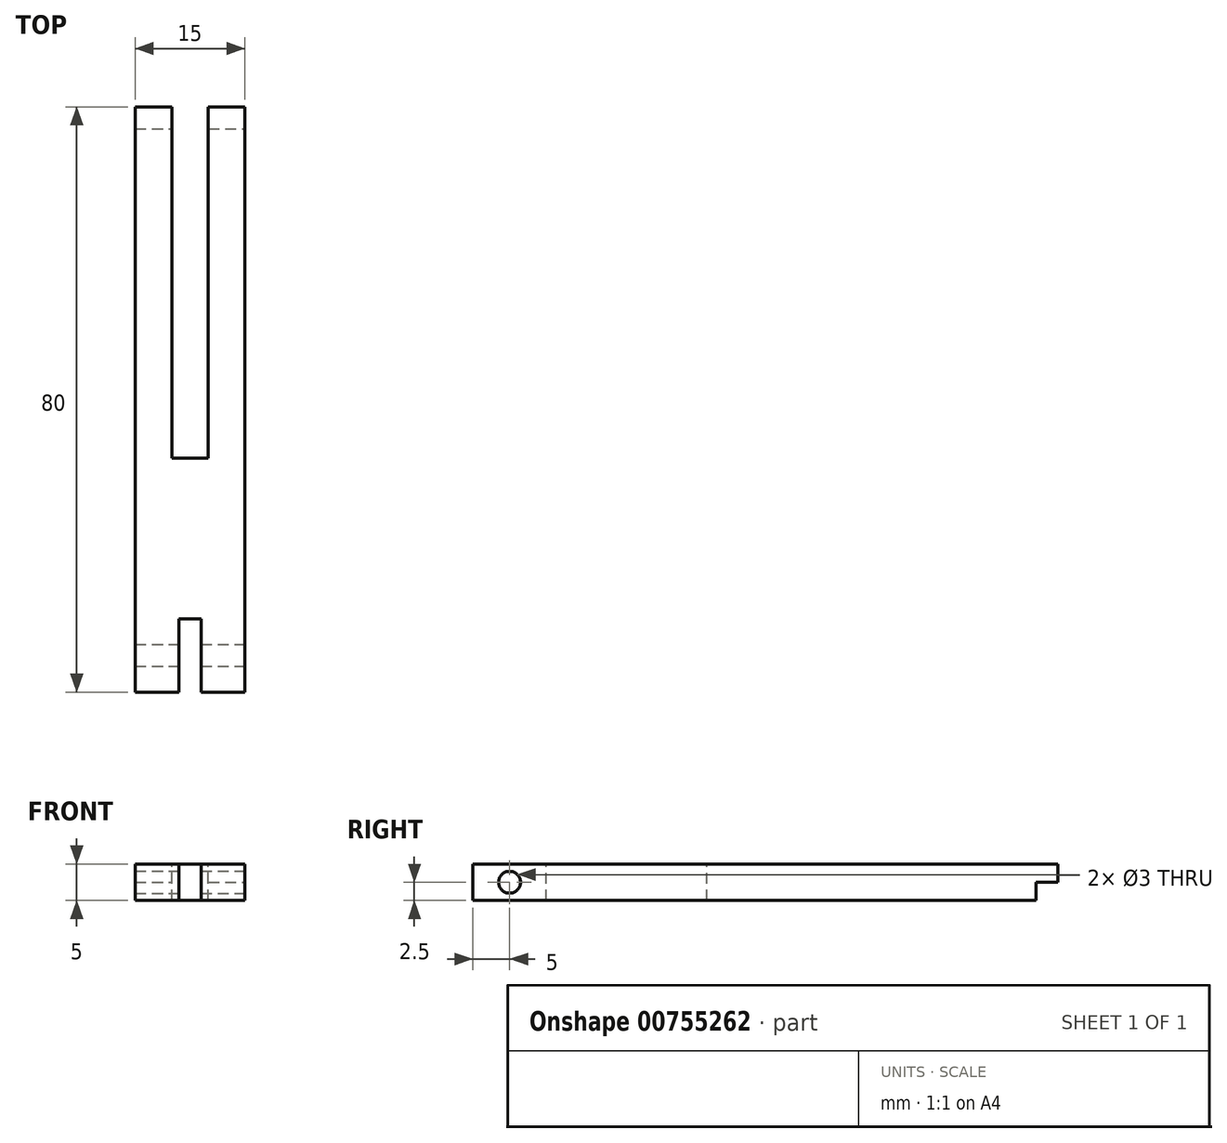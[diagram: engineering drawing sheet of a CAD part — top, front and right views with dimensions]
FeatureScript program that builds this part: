
annotation { "Feature Type Name" : "Feature", "Feature Type Description" : "" }
export const myFeature = defineFeature(function(context is Context, id is Id, definition is map)
    precondition{}
    {
        {
            var Q0;
            Q0=qCreatedBy(makeId("Top.planeOp"),FACE);
            var sketch = newSketch(context, id + "F0", { "sketchPlane" : qUnion([Q0])});
            skLineSegment(sketch, "E0.bottom", {"start": v(-7.5, 80) * mm, "end": v(7.5, 80) * mm});
            skLineSegment(sketch, "E0.top", {"start": v(-7.5, 0) * mm, "end": v(7.5, 0) * mm});
            skLineSegment(sketch, "E0.left", {"start": v(-7.5, 80) * mm, "end": v(-7.5, 0) * mm});
            skLineSegment(sketch, "E0.right", {"start": v(7.5, 80) * mm, "end": v(7.5, 0) * mm});
            skPoint(sketch, "E1", {"position": v(0, 0) * mm});
            skSolve(sketch);
        }
        {
            var Q0;
            Q0 = qSketchRegion(id + "F0", true);
            extrude(context, id + "F1", {"entities" : qUnion([Q0]), "depth" : 5 * mm, "offsetDistance" : 25 * mm});
        }
        {
            var Q0;
            Q0=makeQuery(id+"F1.opExtrude","CAP_FACE",FACE,{"disambiguationData":[OSD([sQuery(id+"F0.wireOp",EDGE,"E0.bottom"),sQuery(id+"F0.wireOp",EDGE,"E0.top"),sQuery(id+"F0.wireOp",EDGE,"E0.left"),sQuery(id+"F0.wireOp",EDGE,"E0.right")])],"isStart":false});
            var sketch = newSketch(context, id + "F2", { "sketchPlane" : qUnion([Q0])});
            skLineSegment(sketch, "E2.bottom", {"start": v(-2.5, 80) * mm, "end": v(2.5, 80) * mm});
            skLineSegment(sketch, "E2.top", {"start": v(-2.5, 32) * mm, "end": v(2.5, 32) * mm});
            skLineSegment(sketch, "E2.left", {"start": v(-2.5, 80) * mm, "end": v(-2.5, 32) * mm});
            skLineSegment(sketch, "E2.right", {"start": v(2.5, 80) * mm, "end": v(2.5, 32) * mm});
            skPoint(sketch, "E3", {"position": v(0, 32) * mm});
            skSolve(sketch);
        }
        {
            var Q0;
            Q0=makeQuery(id+"F2.imprint","IMPRINT",FACE,{"disambiguationData":[TD([[makeQuery(id+"F2.imprint","IMPRINT",EDGE,{"derivedFrom":sQuery(id+"F2.wireOp",EDGE,"E2.bottom")}),-1.0]])]});
            extrude(context, id + "F3", {"entities" : qUnion([Q0]), "operationType" : NewBodyOperationType.REMOVE, "oppositeDirection" : true, "depth" : 25 * mm, "offsetDistance" : 25 * mm});
        }
        {
            var Q0;
            {var subQ1=sQuery(id+"F0.wireOp",EDGE,"E0.left");var subQ3=sQuery(id+"F0.wireOp",EDGE,"E0.bottom");Q0=makeQuery(id+"F3.boolean.opBoolean","SPLIT",FACE,{"disambiguationData":[TD([makeQuery(id+"F1.opExtrude","SWEPT_FACE",FACE,{"disambiguationData":[OSD([subQ1])]})])],"derivedFrom":makeQuery(id+"F1.opExtrude","SWEPT_FACE",FACE,{"disambiguationData":[OSD([subQ3])]})});}
            var sketch = newSketch(context, id + "F4", { "sketchPlane" : qUnion([Q0])});
            skLineSegment(sketch, "E4.bottom", {"start": v(7.5, 2.5) * mm, "end": v(2.5, 2.5) * mm});
            skLineSegment(sketch, "E4.top", {"start": v(7.5, 0) * mm, "end": v(2.5, 0) * mm});
            skLineSegment(sketch, "E4.left", {"start": v(7.5, 2.5) * mm, "end": v(7.5, 0) * mm});
            skLineSegment(sketch, "E4.right", {"start": v(2.5, 2.5) * mm, "end": v(2.5, 0) * mm});
            skSolve(sketch);
        }
        {
            var Q0;
            Q0=makeQuery(id+"F4.imprint","IMPRINT",FACE,{"disambiguationData":[TD([[makeQuery(id+"F4.imprint","IMPRINT",EDGE,{"derivedFrom":sQuery(id+"F4.wireOp",EDGE,"E4.bottom")}),1.0]])]});
            extrude(context, id + "F5", {"entities" : qUnion([Q0]), "operationType" : NewBodyOperationType.REMOVE, "oppositeDirection" : true, "depth" : 3 * mm, "offsetDistance" : 25 * mm});
        }
        {
            var Q0;
            {var subQ0=sQuery(id+"F0.wireOp",EDGE,"E0.right");var subQ3=sQuery(id+"F0.wireOp",EDGE,"E0.bottom");Q0=makeQuery(id+"F3.boolean.opBoolean","SPLIT",FACE,{"disambiguationData":[TD([makeQuery(id+"F1.opExtrude","SWEPT_FACE",FACE,{"disambiguationData":[OSD([subQ0])]})])],"derivedFrom":makeQuery(id+"F1.opExtrude","SWEPT_FACE",FACE,{"disambiguationData":[OSD([subQ3])]})});}
            var sketch = newSketch(context, id + "F6", { "sketchPlane" : qUnion([Q0])});
            skLineSegment(sketch, "E5.bottom", {"start": v(-2.5, 0) * mm, "end": v(-7.5, 0) * mm});
            skLineSegment(sketch, "E5.top", {"start": v(-2.5, 2.5) * mm, "end": v(-7.5, 2.5) * mm});
            skLineSegment(sketch, "E5.left", {"start": v(-2.5, 0) * mm, "end": v(-2.5, 2.5) * mm});
            skLineSegment(sketch, "E5.right", {"start": v(-7.5, 0) * mm, "end": v(-7.5, 2.5) * mm});
            skSolve(sketch);
        }
        {
            var Q0;
            Q0=makeQuery(id+"F6.imprint","IMPRINT",FACE,{"disambiguationData":[TD([[makeQuery(id+"F6.imprint","IMPRINT",EDGE,{"derivedFrom":sQuery(id+"F6.wireOp",EDGE,"E5.bottom")}),-1.0]])]});
            extrude(context, id + "F7", {"entities" : qUnion([Q0]), "operationType" : NewBodyOperationType.REMOVE, "oppositeDirection" : true, "depth" : 3 * mm, "offsetDistance" : 25 * mm});
        }
        {
            var Q0;
            Q0=makeQuery(id+"F1.opExtrude","CAP_FACE",FACE,{"disambiguationData":[OSD([sQuery(id+"F0.wireOp",EDGE,"E0.bottom"),sQuery(id+"F0.wireOp",EDGE,"E0.top"),sQuery(id+"F0.wireOp",EDGE,"E0.left"),sQuery(id+"F0.wireOp",EDGE,"E0.right")])],"isStart":false});
            var sketch = newSketch(context, id + "F8", { "sketchPlane" : qUnion([Q0])});
            skLineSegment(sketch, "E6.bottom", {"start": v(-1.5, 0) * mm, "end": v(1.5, 0) * mm});
            skLineSegment(sketch, "E6.top", {"start": v(-1.5, 10) * mm, "end": v(1.5, 10) * mm});
            skLineSegment(sketch, "E6.left", {"start": v(-1.5, 0) * mm, "end": v(-1.5, 10) * mm});
            skLineSegment(sketch, "E6.right", {"start": v(1.5, 0) * mm, "end": v(1.5, 10) * mm});
            skSolve(sketch);
        }
        {
            var Q0;
            Q0=makeQuery(id+"F8.imprint","IMPRINT",FACE,{"disambiguationData":[TD([[makeQuery(id+"F8.imprint","IMPRINT",EDGE,{"derivedFrom":sQuery(id+"F8.wireOp",EDGE,"E6.bottom")}),1.0]])]});
            extrude(context, id + "F9", {"entities" : qUnion([Q0]), "operationType" : NewBodyOperationType.REMOVE, "oppositeDirection" : true, "depth" : 25 * mm, "offsetDistance" : 25 * mm});
        }
        {
            var Q0;
            Q0=makeQuery(id+"F1.opExtrude","SWEPT_FACE",FACE,{"disambiguationData":[OSD([sQuery(id+"F0.wireOp",EDGE,"E0.right")])]});
            var sketch = newSketch(context, id + "F10", { "sketchPlane" : qUnion([Q0])});
            skLineSegment(sketch, "E7.bottom", {"start": v(0, 5) * mm, "end": v(10, 5) * mm});
            skLineSegment(sketch, "E7.top", {"start": v(0, 0) * mm, "end": v(10, 0) * mm});
            skLineSegment(sketch, "E7.left", {"start": v(0, 5) * mm, "end": v(0, 0) * mm});
            skLineSegment(sketch, "E7.right", {"start": v(10, 5) * mm, "end": v(10, 0) * mm});
            skPoint(sketch, "E8", {"position": v(5, 2.5) * mm});
            skPoint(sketch, "E8.positionSnap0", {"position": v(5, 5) * mm});
            skPoint(sketch, "E8.positionSnap1", {"position": v(10, 2.5) * mm});
            skSolve(sketch);
        }
        {
            var Q0;
            Q0=sQuery(id+"F10.wireOp",VERTEX,"E8");
            var Q1;
            Q1=makeQuery(id+"F1.opExtrude","SWEPT_BODY",BODY,{"disambiguationData":[OSD([sQuery(id+"F0.wireOp",EDGE,"E0.bottom"),sQuery(id+"F0.wireOp",EDGE,"E0.top"),sQuery(id+"F0.wireOp",EDGE,"E0.left"),sQuery(id+"F0.wireOp",EDGE,"E0.right")])]});
            hole(context, id + "F11", {"style" : HoleStyle.SIMPLE, "endStyle" : HoleEndStyle.THROUGH, "holeDiameter" : 3 * mm, "majorDiameter" : 5 * mm, "isTappedThrough" : true, "tappedDepth" : 12 * mm, "tapClearance" : 3, "locations" : qUnion([Q0]), "scope" : qUnion([Q1])});
        }
    });
